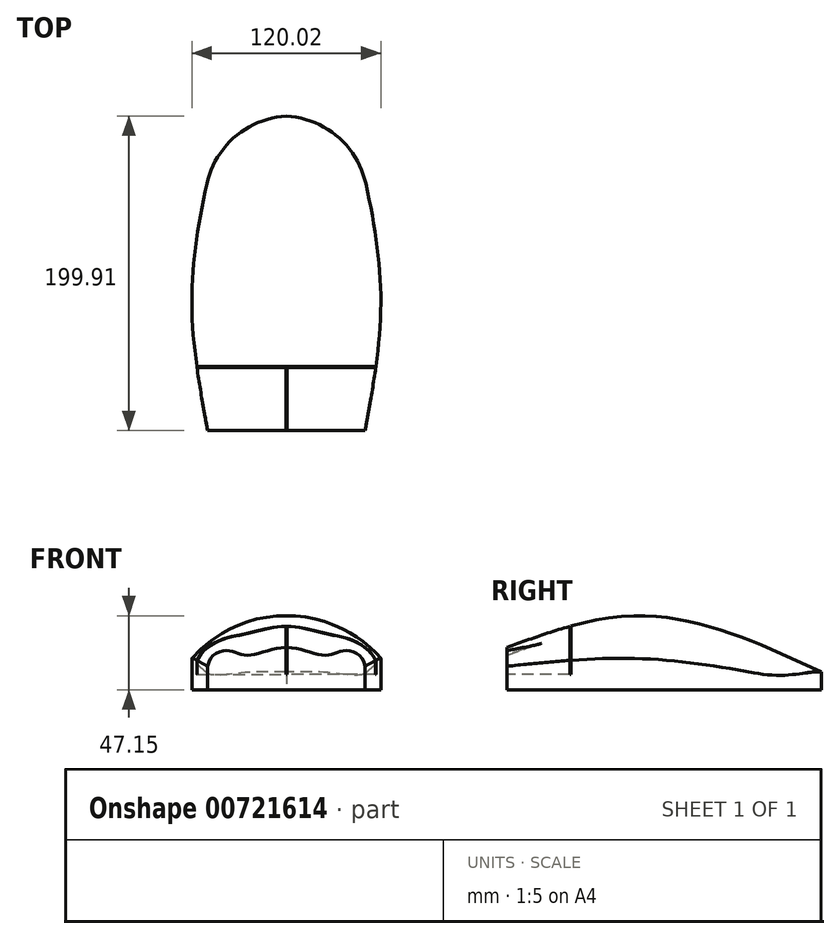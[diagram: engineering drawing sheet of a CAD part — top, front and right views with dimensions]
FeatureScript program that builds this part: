
annotation { "Feature Type Name" : "Feature", "Feature Type Description" : "" }
export const myFeature = defineFeature(function(context is Context, id is Id, definition is map)
    precondition{}
    {
        {
            var Q0;
            Q0=qCreatedBy(makeId("Front.planeOp"),FACE);
            var sketch = newSketch(context, id + "F0", { "sketchPlane" : qUnion([Q0])});
            skLineSegment(sketch, "E0", {"start": v(-40, 0) * mm, "end": v(40, 0) * mm});
            skLineSegment(sketch, "E1", {"start": v(40, 0) * mm, "end": v(40, 2) * mm});
            skLineSegment(sketch, "E2", {"start": v(-40, 0) * mm, "end": v(-40, 2) * mm});
            skArc(sketch, "E3", {"start": v(40, 2) * mm, "mid": v(0, 11.38) * mm, "end": v(-40, 2) * mm});
            skSolve(sketch);
        }
        {
            var Q0;
            Q0=qCreatedBy(makeId("Front.planeOp"),FACE);
            cPlane(context, id + "F1", {"entities" : qUnion([Q0]), "cplaneType" : CPlaneType.OFFSET, "offset" : 120 * mm, "width" : 150 * mm, "height" : 150 * mm});
        }
        {
            var Q0;
            Q0=qCreatedBy(id+"F1.planeOp",FACE);
            cPlane(context, id + "F2", {"entities" : qUnion([Q0]), "cplaneType" : CPlaneType.OFFSET, "offset" : 80 * mm, "width" : 150 * mm, "height" : 150 * mm});
        }
        {
            var Q0;
            Q0=qCreatedBy(id+"F1.planeOp",FACE);
            var sketch = newSketch(context, id + "F3", { "sketchPlane" : qUnion([Q0])});
            skLineSegment(sketch, "E4", {"start": v(-60, 0) * mm, "end": v(60, 0) * mm});
            skLineSegment(sketch, "E5", {"start": v(60, 0) * mm, "end": v(60, 20) * mm});
            skLineSegment(sketch, "E6", {"start": v(-60, 0) * mm, "end": v(-60, 20) * mm});
            skArc(sketch, "E7", {"start": v(60, 20) * mm, "mid": v(0, 47.08) * mm, "end": v(-60, 20) * mm});
            skSolve(sketch);
        }
        {
            var Q0;
            Q0=qCreatedBy(id+"F2.planeOp",FACE);
            var sketch = newSketch(context, id + "F4", { "sketchPlane" : qUnion([Q0])});
            skLineSegment(sketch, "E8", {"start": v(-50, 0) * mm, "end": v(50, 0) * mm});
            skLineSegment(sketch, "E9", {"start": v(50, 0) * mm, "end": v(50, 15) * mm});
            skLineSegment(sketch, "E10", {"start": v(-50, 0) * mm, "end": v(-50, 15) * mm});
            skLineSegment(sketch, "E11", {"start": v(-25, 0) * mm, "end": v(-25, 22) * mm, "construction": true});
            skLineSegment(sketch, "E12", {"start": v(25, 0) * mm, "end": v(25, 22) * mm, "construction": true});
            skLineSegment(sketch, "E13", {"start": v(-37.5, 0) * mm, "end": v(-37.5, 25) * mm, "construction": true});
            skLineSegment(sketch, "E14", {"start": v(37.5, 0) * mm, "end": v(37.5, 25) * mm, "construction": true});
            skFitSpline(sketch, "E15", {"points": [v(-50, 15) * mm, v(-37.5, 25) * mm, v(-25, 22) * mm, v(0, 26.98) * mm, v(25, 22) * mm, v(37.5, 25) * mm, v(50, 15) * mm], "startDerivative": vector(20.98, 139.66) * mm, "endDerivative": vector(18.6, -135.18) * mm});
            skSolve(sketch);
        }
        {
            var Q0;
            Q0=makeQuery(id+"F0.imprint","IMPRINT",FACE,{"disambiguationData":[TD([[makeQuery(id+"F0.imprint","IMPRINT",EDGE,{"derivedFrom":sQuery(id+"F0.wireOp",EDGE,"E0")}),1.0]])]});
            var Q1;
            Q1=makeQuery(id+"F3.imprint","IMPRINT",FACE,{"disambiguationData":[TD([[makeQuery(id+"F3.imprint","IMPRINT",EDGE,{"derivedFrom":sQuery(id+"F3.wireOp",EDGE,"E4")}),1.0]])]});
            var Q2;
            Q2=makeQuery(id+"F4.imprint","IMPRINT",FACE,{"disambiguationData":[TD([[makeQuery(id+"F4.imprint","IMPRINT",EDGE,{"derivedFrom":sQuery(id+"F4.wireOp",EDGE,"E8")}),1.0]])]});
            loft(context, id + "F5", {"sheetProfilesArray" : [{ "sheetProfileEntities" : qUnion([Q0]) }, { "sheetProfileEntities" : qUnion([Q1]) }, { "sheetProfileEntities" : qUnion([Q2]) }]});
        }
        {
            var Q0;
            Q0=makeQuery(id+"F5.opLoft","MID_CAP_EDGE",EDGE,{"disambiguationData":[OSD([sQuery(id+"F0.wireOp",EDGE,"E0"),sQuery(id+"F0.wireOp",EDGE,"E2"),sQuery(id+"F0.wireOp",EDGE,"E3")])],"capPos":0.0});
            fillet(context, id + "F6", {"entities" : qUnion([Q0]), "radius" : 55 * mm, "tangentPropagation" : true, "allowEdgeOverflow" : false});
        }
        {
            var Q0;
            Q0=makeQuery(id+"F5.opLoft","MID_CAP_EDGE",EDGE,{"disambiguationData":[OSD([sQuery(id+"F0.wireOp",EDGE,"E0"),sQuery(id+"F0.wireOp",EDGE,"E1"),sQuery(id+"F0.wireOp",EDGE,"E3")])],"capPos":0.0});
            fillet(context, id + "F7", {"entities" : qUnion([Q0]), "radius" : 55 * mm, "tangentPropagation" : true, "allowEdgeOverflow" : false});
        }
        {
            var Q0;
            Q0=qCreatedBy(id+"F2.planeOp",FACE);
            var sketch = newSketch(context, id + "F8", { "sketchPlane" : qUnion([Q0])});
            skLineSegment(sketch, "E16", {"start": v(0, 0) * mm, "end": v(0, 10) * mm, "construction": true});
            skLineSegment(sketch, "E17.bottom", {"start": v(-0.35, 10) * mm, "end": v(0.35, 10) * mm});
            skLineSegment(sketch, "E17.top", {"start": v(-0.35, 44) * mm, "end": v(0.35, 44) * mm});
            skLineSegment(sketch, "E17.left", {"start": v(-0.35, 10) * mm, "end": v(-0.35, 44) * mm});
            skLineSegment(sketch, "E17.right", {"start": v(0.35, 10) * mm, "end": v(0.35, 44) * mm});
            skSolve(sketch);
        }
        {
            var Q0;
            Q0=makeQuery(id+"F8.imprint","IMPRINT",FACE,{"disambiguationData":[TD([[makeQuery(id+"F8.imprint","IMPRINT",EDGE,{"derivedFrom":sQuery(id+"F8.wireOp",EDGE,"E17.bottom")}),1.0]])]});
            extrude(context, id + "F9", {"entities" : qUnion([Q0]), "operationType" : NewBodyOperationType.REMOVE, "oppositeDirection" : true, "depth" : 40 * mm, "offsetDistance" : 25 * mm});
        }
        {
            var Q0;
            Q0=qCreatedBy(makeId("Right.planeOp"),FACE);
            var sketch = newSketch(context, id + "F10", { "sketchPlane" : qUnion([Q0])});
            skLineSegment(sketch, "E18.bottom", {"start": v(-160, 10) * mm, "end": v(-159.3, 10) * mm});
            skLineSegment(sketch, "E18.top", {"start": v(-160, 45) * mm, "end": v(-159.3, 45) * mm});
            skLineSegment(sketch, "E18.left", {"start": v(-160, 10) * mm, "end": v(-160, 45) * mm});
            skLineSegment(sketch, "E18.right", {"start": v(-159.3, 10) * mm, "end": v(-159.3, 45) * mm});
            skLineSegment(sketch, "E19", {"start": v(-161.9, 0) * mm, "end": v(-126.82, 0) * mm, "construction": true});
            skSolve(sketch);
        }
        {
            var Q0;
            Q0=qSketchRegion(id+"F10",true);
            extrude(context, id + "F11", {"entities" : qUnion([Q0]), "operationType" : NewBodyOperationType.REMOVE, "oppositeDirection" : true, "depth" : 70 * mm, "offsetDistance" : 25 * mm});
        }
        {
            var Q0;
            Q0=qSketchRegion(id+"F10",true);
            extrude(context, id + "F12", {"entities" : qUnion([Q0]), "operationType" : NewBodyOperationType.REMOVE, "depth" : 70 * mm, "offsetDistance" : 25 * mm});
        }
    });
